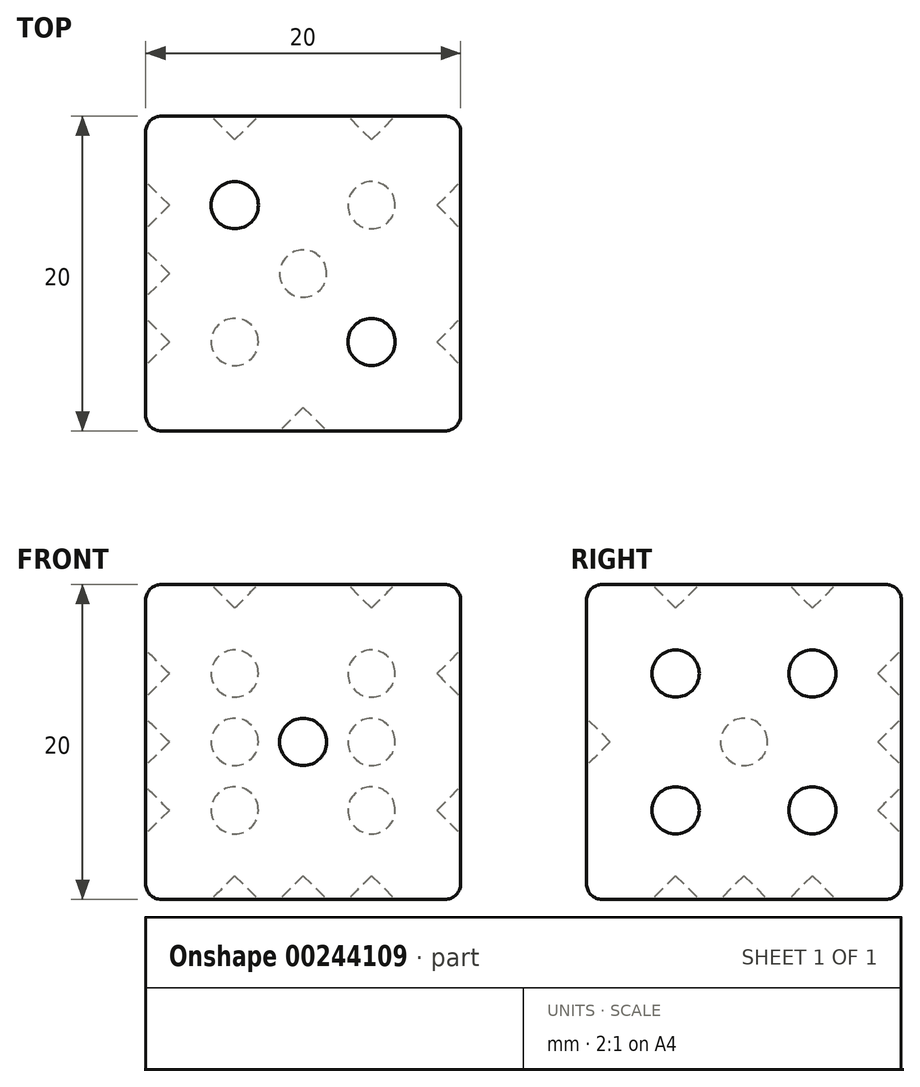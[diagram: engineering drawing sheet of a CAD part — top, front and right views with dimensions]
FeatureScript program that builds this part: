
annotation { "Feature Type Name" : "Feature", "Feature Type Description" : "" }
export const myFeature = defineFeature(function(context is Context, id is Id, definition is map)
    precondition{}
    {
        {
            var Q0;
            Q0=qCreatedBy(makeId("Top.planeOp"),FACE);
            var sketch = newSketch(context, id + "F0", { "sketchPlane" : qUnion([Q0])});
            skLineSegment(sketch, "E0.bottom", {"start": v(0, 0) * mm, "end": v(20, 0) * mm});
            skLineSegment(sketch, "E0.top", {"start": v(0, 20) * mm, "end": v(20, 20) * mm});
            skLineSegment(sketch, "E0.left", {"start": v(0, 0) * mm, "end": v(0, 20) * mm});
            skLineSegment(sketch, "E0.right", {"start": v(20, 0) * mm, "end": v(20, 20) * mm});
            skSolve(sketch);
        }
        {
            var Q0;
            Q0 = qSketchRegion(id + "F0", true);
            extrude(context, id + "F1", {"entities" : qUnion([Q0]), "depth" : 20 * mm});
        }
        {
            var Q0;
            Q0=makeQuery(id+"F1.opExtrude","SWEPT_FACE",FACE,{"disambiguationData":[OSD([sQuery(id+"F0.wireOp",EDGE,"E0.bottom")])]});
            var sketch = newSketch(context, id + "F2", { "sketchPlane" : qUnion([Q0])});
            skLineSegment(sketch, "E1", {"start": v(10, 20) * mm, "end": v(10, 0) * mm, "construction": true});
            skCircle(sketch, "E2", {"center": v(10, 10) * mm, "radius": 1.5 * mm});
            skSolve(sketch);
        }
        {
            var Q0;
            Q0 = qSketchRegion(id + "F2", true);
            extrude(context, id + "F3", {"entities" : qUnion([Q0]), "operationType" : NewBodyOperationType.REMOVE, "oppositeDirection" : true, "depth" : 1.5 * mm});
        }
        {
            var Q0;
            Q0=makeQuery(id+"F3.boolean.opBoolean","COPY",EDGE,{"derivedFrom":makeQuery(id+"F3.opExtrude","CAP_EDGE",EDGE,{"disambiguationData":[OSD([sQuery(id+"F2.wireOp",EDGE,"E2")])],"isStart":false})});
            chamfer(context, id + "F4", {"entities" : qUnion([Q0]), "width" : 1.5 * mm, "tangentPropagation" : true});
        }
        {
            var Q0;
            Q0=makeQuery(id+"F1.opExtrude","CAP_FACE",FACE,{"disambiguationData":[OSD([sQuery(id+"F0.wireOp",EDGE,"E0.bottom"),sQuery(id+"F0.wireOp",EDGE,"E0.top"),sQuery(id+"F0.wireOp",EDGE,"E0.left"),sQuery(id+"F0.wireOp",EDGE,"E0.right")])],"isStart":false});
            var sketch = newSketch(context, id + "F5", { "sketchPlane" : qUnion([Q0])});
            skLineSegment(sketch, "E3", {"start": v(20, 0) * mm, "end": v(14.34, 5.66) * mm, "construction": true});
            skLineSegment(sketch, "E4", {"start": v(0, 20) * mm, "end": v(5.66, 14.34) * mm, "construction": true});
            skCircle(sketch, "E5", {"center": v(5.66, 14.34) * mm, "radius": 1.5 * mm});
            skCircle(sketch, "E6", {"center": v(14.34, 5.66) * mm, "radius": 1.5 * mm});
            skSolve(sketch);
        }
        {
            var Q0;
            Q0=makeQuery(id+"F5.imprint","IMPRINT",FACE,{"disambiguationData":[TD([[makeQuery(id+"F5.imprint","IMPRINT",EDGE,{"derivedFrom":sQuery(id+"F5.wireOp",EDGE,"E5")}),1.0]])]});
            var Q1;
            Q1=makeQuery(id+"F5.imprint","IMPRINT",FACE,{"disambiguationData":[TD([[makeQuery(id+"F5.imprint","IMPRINT",EDGE,{"derivedFrom":sQuery(id+"F5.wireOp",EDGE,"E6")}),1.0]])]});
            extrude(context, id + "F6", {"entities" : qUnion([Q0, Q1]), "operationType" : NewBodyOperationType.REMOVE, "oppositeDirection" : true, "depth" : 1.5 * mm});
        }
        {
            var Q0;
            Q0=makeQuery(id+"F6.boolean.opBoolean","COPY",FACE,{"derivedFrom":makeQuery(id+"F6.opExtrude","CAP_FACE",FACE,{"disambiguationData":[OSD([sQuery(id+"F5.wireOp",EDGE,"E5")])],"isStart":false})});
            chamfer(context, id + "F7", {"entities" : qUnion([Q0]), "width" : 1.5 * mm, "tangentPropagation" : true});
        }
        {
            var Q0;
            Q0=makeQuery(id+"F6.boolean.opBoolean","COPY",FACE,{"derivedFrom":makeQuery(id+"F6.opExtrude","CAP_FACE",FACE,{"disambiguationData":[OSD([sQuery(id+"F5.wireOp",EDGE,"E6")])],"isStart":false})});
            chamfer(context, id + "F8", {"entities" : qUnion([Q0]), "width" : 1.5 * mm, "tangentPropagation" : true});
        }
        {
            var Q0;
            Q0=makeQuery(id+"F1.opExtrude","SWEPT_FACE",FACE,{"disambiguationData":[OSD([sQuery(id+"F0.wireOp",EDGE,"E0.left")])]});
            var sketch = newSketch(context, id + "F9", { "sketchPlane" : qUnion([Q0])});
            skCircle(sketch, "E7", {"center": v(-14.34, 14.34) * mm, "radius": 1.5 * mm});
            skCircle(sketch, "E8", {"center": v(-5.66, 5.66) * mm, "radius": 1.5 * mm});
            skCircle(sketch, "E9", {"center": v(-10, 10) * mm, "radius": 1.5 * mm});
            skSolve(sketch);
        }
        {
            var Q0;
            Q0=makeQuery(id+"F9.imprint","IMPRINT",FACE,{"disambiguationData":[TD([[makeQuery(id+"F9.imprint","IMPRINT",EDGE,{"derivedFrom":sQuery(id+"F9.wireOp",EDGE,"E7")}),1.0]])]});
            var Q1;
            Q1=makeQuery(id+"F9.imprint","IMPRINT",FACE,{"disambiguationData":[TD([[makeQuery(id+"F9.imprint","IMPRINT",EDGE,{"derivedFrom":sQuery(id+"F9.wireOp",EDGE,"E9")}),1.0]])]});
            var Q2;
            Q2=makeQuery(id+"F9.imprint","IMPRINT",FACE,{"disambiguationData":[TD([[makeQuery(id+"F9.imprint","IMPRINT",EDGE,{"derivedFrom":sQuery(id+"F9.wireOp",EDGE,"E8")}),1.0]])]});
            extrude(context, id + "F10", {"entities" : qUnion([Q0, Q1, Q2]), "operationType" : NewBodyOperationType.REMOVE, "oppositeDirection" : true, "depth" : 1.5 * mm});
        }
        {
            var Q0;
            Q0=makeQuery(id+"F10.boolean.opBoolean","COPY",FACE,{"derivedFrom":makeQuery(id+"F10.opExtrude","CAP_FACE",FACE,{"disambiguationData":[OSD([sQuery(id+"F9.wireOp",EDGE,"E7")])],"isStart":false})});
            var Q1;
            Q1=makeQuery(id+"F10.boolean.opBoolean","COPY",FACE,{"derivedFrom":makeQuery(id+"F10.opExtrude","CAP_FACE",FACE,{"disambiguationData":[OSD([sQuery(id+"F9.wireOp",EDGE,"E9")])],"isStart":false})});
            var Q2;
            Q2=makeQuery(id+"F10.boolean.opBoolean","COPY",FACE,{"derivedFrom":makeQuery(id+"F10.opExtrude","CAP_FACE",FACE,{"disambiguationData":[OSD([sQuery(id+"F9.wireOp",EDGE,"E8")])],"isStart":false})});
            chamfer(context, id + "F11", {"entities" : qUnion([Q0, Q1, Q2]), "width" : 1.5 * mm, "tangentPropagation" : true});
        }
        {
            var Q0;
            Q0=makeQuery(id+"F1.opExtrude","SWEPT_FACE",FACE,{"disambiguationData":[OSD([sQuery(id+"F0.wireOp",EDGE,"E0.right")])]});
            var sketch = newSketch(context, id + "F12", { "sketchPlane" : qUnion([Q0])});
            skCircle(sketch, "E10", {"center": v(5.66, 14.34) * mm, "radius": 1.5 * mm});
            skCircle(sketch, "E11", {"center": v(14.34, 14.34) * mm, "radius": 1.5 * mm});
            skCircle(sketch, "E12", {"center": v(14.34, 5.66) * mm, "radius": 1.5 * mm});
            skCircle(sketch, "E13", {"center": v(5.66, 5.66) * mm, "radius": 1.5 * mm});
            skSolve(sketch);
        }
        {
            var Q0;
            Q0=makeQuery(id+"F12.imprint","IMPRINT",FACE,{"disambiguationData":[TD([[makeQuery(id+"F12.imprint","IMPRINT",EDGE,{"derivedFrom":sQuery(id+"F12.wireOp",EDGE,"E10")}),1.0]])]});
            var Q1;
            Q1=makeQuery(id+"F12.imprint","IMPRINT",FACE,{"disambiguationData":[TD([[makeQuery(id+"F12.imprint","IMPRINT",EDGE,{"derivedFrom":sQuery(id+"F12.wireOp",EDGE,"E11")}),1.0]])]});
            var Q2;
            Q2=makeQuery(id+"F12.imprint","IMPRINT",FACE,{"disambiguationData":[TD([[makeQuery(id+"F12.imprint","IMPRINT",EDGE,{"derivedFrom":sQuery(id+"F12.wireOp",EDGE,"E12")}),1.0]])]});
            var Q3;
            Q3=makeQuery(id+"F12.imprint","IMPRINT",FACE,{"disambiguationData":[TD([[makeQuery(id+"F12.imprint","IMPRINT",EDGE,{"derivedFrom":sQuery(id+"F12.wireOp",EDGE,"E13")}),1.0]])]});
            extrude(context, id + "F13", {"entities" : qUnion([Q0, Q1, Q2, Q3]), "operationType" : NewBodyOperationType.REMOVE, "oppositeDirection" : true, "depth" : 1.5 * mm});
        }
        {
            var Q0;
            Q0=makeQuery(id+"F13.boolean.opBoolean","COPY",FACE,{"derivedFrom":makeQuery(id+"F13.opExtrude","CAP_FACE",FACE,{"disambiguationData":[OSD([sQuery(id+"F12.wireOp",EDGE,"E10")])],"isStart":false})});
            var Q1;
            Q1=makeQuery(id+"F13.boolean.opBoolean","COPY",FACE,{"derivedFrom":makeQuery(id+"F13.opExtrude","CAP_FACE",FACE,{"disambiguationData":[OSD([sQuery(id+"F12.wireOp",EDGE,"E11")])],"isStart":false})});
            var Q2;
            Q2=makeQuery(id+"F13.boolean.opBoolean","COPY",FACE,{"derivedFrom":makeQuery(id+"F13.opExtrude","CAP_FACE",FACE,{"disambiguationData":[OSD([sQuery(id+"F12.wireOp",EDGE,"E12")])],"isStart":false})});
            var Q3;
            Q3=makeQuery(id+"F13.boolean.opBoolean","COPY",FACE,{"derivedFrom":makeQuery(id+"F13.opExtrude","CAP_FACE",FACE,{"disambiguationData":[OSD([sQuery(id+"F12.wireOp",EDGE,"E13")])],"isStart":false})});
            chamfer(context, id + "F14", {"entities" : qUnion([Q0, Q1, Q2, Q3]), "width" : 1.5 * mm, "tangentPropagation" : true});
        }
        {
            var Q0;
            Q0=makeQuery(id+"F1.opExtrude","CAP_FACE",FACE,{"disambiguationData":[OSD([sQuery(id+"F0.wireOp",EDGE,"E0.bottom"),sQuery(id+"F0.wireOp",EDGE,"E0.top"),sQuery(id+"F0.wireOp",EDGE,"E0.left"),sQuery(id+"F0.wireOp",EDGE,"E0.right")])],"isStart":true});
            var sketch = newSketch(context, id + "F15", { "sketchPlane" : qUnion([Q0])});
            skCircle(sketch, "E14", {"center": v(5.66, -5.66) * mm, "radius": 1.5 * mm});
            skCircle(sketch, "E15", {"center": v(14.34, -5.66) * mm, "radius": 1.5 * mm});
            skCircle(sketch, "E16", {"center": v(14.34, -14.34) * mm, "radius": 1.5 * mm});
            skCircle(sketch, "E17", {"center": v(5.66, -14.34) * mm, "radius": 1.5 * mm});
            skCircle(sketch, "E18", {"center": v(10, -10) * mm, "radius": 1.5 * mm});
            skSolve(sketch);
        }
        {
            var Q0;
            Q0=makeQuery(id+"F15.imprint","IMPRINT",FACE,{"disambiguationData":[TD([[makeQuery(id+"F15.imprint","IMPRINT",EDGE,{"derivedFrom":sQuery(id+"F15.wireOp",EDGE,"E14")}),1.0]])]});
            var Q1;
            Q1=makeQuery(id+"F15.imprint","IMPRINT",FACE,{"disambiguationData":[TD([[makeQuery(id+"F15.imprint","IMPRINT",EDGE,{"derivedFrom":sQuery(id+"F15.wireOp",EDGE,"E18")}),1.0]])]});
            var Q2;
            Q2=makeQuery(id+"F15.imprint","IMPRINT",FACE,{"disambiguationData":[TD([[makeQuery(id+"F15.imprint","IMPRINT",EDGE,{"derivedFrom":sQuery(id+"F15.wireOp",EDGE,"E15")}),1.0]])]});
            var Q3;
            Q3=makeQuery(id+"F15.imprint","IMPRINT",FACE,{"disambiguationData":[TD([[makeQuery(id+"F15.imprint","IMPRINT",EDGE,{"derivedFrom":sQuery(id+"F15.wireOp",EDGE,"E16")}),1.0]])]});
            var Q4;
            Q4=makeQuery(id+"F15.imprint","IMPRINT",FACE,{"disambiguationData":[TD([[makeQuery(id+"F15.imprint","IMPRINT",EDGE,{"derivedFrom":sQuery(id+"F15.wireOp",EDGE,"E17")}),1.0]])]});
            extrude(context, id + "F16", {"entities" : qUnion([Q0, Q1, Q2, Q3, Q4]), "operationType" : NewBodyOperationType.REMOVE, "oppositeDirection" : true, "depth" : 1.5 * mm});
        }
        {
            var Q0;
            Q0=makeQuery(id+"F16.boolean.opBoolean","COPY",FACE,{"derivedFrom":makeQuery(id+"F16.opExtrude","CAP_FACE",FACE,{"disambiguationData":[OSD([sQuery(id+"F15.wireOp",EDGE,"E14")])],"isStart":false})});
            var Q1;
            Q1=makeQuery(id+"F16.boolean.opBoolean","COPY",FACE,{"derivedFrom":makeQuery(id+"F16.opExtrude","CAP_FACE",FACE,{"disambiguationData":[OSD([sQuery(id+"F15.wireOp",EDGE,"E15")])],"isStart":false})});
            var Q2;
            Q2=makeQuery(id+"F16.boolean.opBoolean","COPY",FACE,{"derivedFrom":makeQuery(id+"F16.opExtrude","CAP_FACE",FACE,{"disambiguationData":[OSD([sQuery(id+"F15.wireOp",EDGE,"E18")])],"isStart":false})});
            var Q3;
            Q3=makeQuery(id+"F16.boolean.opBoolean","COPY",FACE,{"derivedFrom":makeQuery(id+"F16.opExtrude","CAP_FACE",FACE,{"disambiguationData":[OSD([sQuery(id+"F15.wireOp",EDGE,"E17")])],"isStart":false})});
            var Q4;
            Q4=makeQuery(id+"F16.boolean.opBoolean","COPY",FACE,{"derivedFrom":makeQuery(id+"F16.opExtrude","CAP_FACE",FACE,{"disambiguationData":[OSD([sQuery(id+"F15.wireOp",EDGE,"E16")])],"isStart":false})});
            chamfer(context, id + "F17", {"entities" : qUnion([Q0, Q1, Q2, Q3, Q4]), "width" : 1.5 * mm, "tangentPropagation" : true});
        }
        {
            var Q0;
            Q0=makeQuery(id+"F1.opExtrude","SWEPT_FACE",FACE,{"disambiguationData":[OSD([sQuery(id+"F0.wireOp",EDGE,"E0.top")])]});
            var sketch = newSketch(context, id + "F18", { "sketchPlane" : qUnion([Q0])});
            skCircle(sketch, "E19", {"center": v(-14.34, 14.34) * mm, "radius": 1.5 * mm});
            skCircle(sketch, "E20", {"center": v(-5.66, 14.34) * mm, "radius": 1.5 * mm});
            skCircle(sketch, "E21", {"center": v(-5.66, 5.66) * mm, "radius": 1.5 * mm});
            skCircle(sketch, "E22", {"center": v(-14.34, 5.66) * mm, "radius": 1.5 * mm});
            skCircle(sketch, "E23", {"center": v(-14.34, 10) * mm, "radius": 1.5 * mm});
            skCircle(sketch, "E24", {"center": v(-5.66, 10) * mm, "radius": 1.5 * mm});
            skSolve(sketch);
        }
        {
            var Q0;
            Q0=makeQuery(id+"F18.imprint","IMPRINT",FACE,{"disambiguationData":[TD([[makeQuery(id+"F18.imprint","IMPRINT",EDGE,{"derivedFrom":sQuery(id+"F18.wireOp",EDGE,"E19")}),1.0]])]});
            var Q1;
            Q1=makeQuery(id+"F18.imprint","IMPRINT",FACE,{"disambiguationData":[TD([[makeQuery(id+"F18.imprint","IMPRINT",EDGE,{"derivedFrom":sQuery(id+"F18.wireOp",EDGE,"E20")}),1.0]])]});
            var Q2;
            Q2=makeQuery(id+"F18.imprint","IMPRINT",FACE,{"disambiguationData":[TD([[makeQuery(id+"F18.imprint","IMPRINT",EDGE,{"derivedFrom":sQuery(id+"F18.wireOp",EDGE,"E24")}),1.0]])]});
            var Q3;
            Q3=makeQuery(id+"F18.imprint","IMPRINT",FACE,{"disambiguationData":[TD([[makeQuery(id+"F18.imprint","IMPRINT",EDGE,{"derivedFrom":sQuery(id+"F18.wireOp",EDGE,"E23")}),1.0]])]});
            var Q4;
            Q4=makeQuery(id+"F18.imprint","IMPRINT",FACE,{"disambiguationData":[TD([[makeQuery(id+"F18.imprint","IMPRINT",EDGE,{"derivedFrom":sQuery(id+"F18.wireOp",EDGE,"E22")}),1.0]])]});
            var Q5;
            Q5=makeQuery(id+"F18.imprint","IMPRINT",FACE,{"disambiguationData":[TD([[makeQuery(id+"F18.imprint","IMPRINT",EDGE,{"derivedFrom":sQuery(id+"F18.wireOp",EDGE,"E21")}),1.0]])]});
            extrude(context, id + "F19", {"entities" : qUnion([Q0, Q1, Q2, Q3, Q4, Q5]), "operationType" : NewBodyOperationType.REMOVE, "oppositeDirection" : true, "depth" : 1.5 * mm});
        }
        {
            var Q0;
            Q0=makeQuery(id+"F19.boolean.opBoolean","COPY",FACE,{"derivedFrom":makeQuery(id+"F19.opExtrude","CAP_FACE",FACE,{"disambiguationData":[OSD([sQuery(id+"F18.wireOp",EDGE,"E19")])],"isStart":false})});
            var Q1;
            Q1=makeQuery(id+"F19.boolean.opBoolean","COPY",FACE,{"derivedFrom":makeQuery(id+"F19.opExtrude","CAP_FACE",FACE,{"disambiguationData":[OSD([sQuery(id+"F18.wireOp",EDGE,"E20")])],"isStart":false})});
            var Q2;
            Q2=makeQuery(id+"F19.boolean.opBoolean","COPY",FACE,{"derivedFrom":makeQuery(id+"F19.opExtrude","CAP_FACE",FACE,{"disambiguationData":[OSD([sQuery(id+"F18.wireOp",EDGE,"E24")])],"isStart":false})});
            var Q3;
            Q3=makeQuery(id+"F19.boolean.opBoolean","COPY",FACE,{"derivedFrom":makeQuery(id+"F19.opExtrude","CAP_FACE",FACE,{"disambiguationData":[OSD([sQuery(id+"F18.wireOp",EDGE,"E23")])],"isStart":false})});
            var Q4;
            Q4=makeQuery(id+"F19.boolean.opBoolean","COPY",FACE,{"derivedFrom":makeQuery(id+"F19.opExtrude","CAP_FACE",FACE,{"disambiguationData":[OSD([sQuery(id+"F18.wireOp",EDGE,"E22")])],"isStart":false})});
            var Q5;
            Q5=makeQuery(id+"F19.boolean.opBoolean","COPY",FACE,{"derivedFrom":makeQuery(id+"F19.opExtrude","CAP_FACE",FACE,{"disambiguationData":[OSD([sQuery(id+"F18.wireOp",EDGE,"E21")])],"isStart":false})});
            chamfer(context, id + "F20", {"entities" : qUnion([Q0, Q1, Q2, Q3, Q4, Q5]), "width" : 1.5 * mm, "tangentPropagation" : true});
        }
        {
            var Q0;
            Q0=makeQuery(id+"F1.opExtrude","CAP_EDGE",EDGE,{"disambiguationData":[OSD([sQuery(id+"F0.wireOp",EDGE,"E0.left")])],"isStart":false});
            var Q1;
            Q1=makeQuery(id+"F1.opExtrude","CAP_EDGE",EDGE,{"disambiguationData":[OSD([sQuery(id+"F0.wireOp",EDGE,"E0.bottom")])],"isStart":false});
            var Q2;
            Q2=makeQuery(id+"F1.opExtrude","CAP_EDGE",EDGE,{"disambiguationData":[OSD([sQuery(id+"F0.wireOp",EDGE,"E0.right")])],"isStart":false});
            var Q3;
            Q3=makeQuery(id+"F1.opExtrude","CAP_EDGE",EDGE,{"disambiguationData":[OSD([sQuery(id+"F0.wireOp",EDGE,"E0.top")])],"isStart":false});
            var Q4;
            Q4=makeQuery(id+"F1.opExtrude","SWEPT_EDGE",EDGE,{"disambiguationData":[OSD([sQuery(id+"F0.wireOp",EDGE,"E0.top"),sQuery(id+"F0.wireOp",EDGE,"E0.right")])]});
            var Q5;
            Q5=makeQuery(id+"F1.opExtrude","SWEPT_EDGE",EDGE,{"disambiguationData":[OSD([sQuery(id+"F0.wireOp",EDGE,"E0.bottom"),sQuery(id+"F0.wireOp",EDGE,"E0.right")])]});
            var Q6;
            Q6=makeQuery(id+"F1.opExtrude","SWEPT_EDGE",EDGE,{"disambiguationData":[OSD([sQuery(id+"F0.wireOp",EDGE,"E0.bottom"),sQuery(id+"F0.wireOp",EDGE,"E0.left")])]});
            var Q7;
            Q7=makeQuery(id+"F1.opExtrude","CAP_EDGE",EDGE,{"disambiguationData":[OSD([sQuery(id+"F0.wireOp",EDGE,"E0.right")])],"isStart":true});
            var Q8;
            Q8=makeQuery(id+"F1.opExtrude","CAP_EDGE",EDGE,{"disambiguationData":[OSD([sQuery(id+"F0.wireOp",EDGE,"E0.bottom")])],"isStart":true});
            var Q9;
            Q9=makeQuery(id+"F1.opExtrude","SWEPT_EDGE",EDGE,{"disambiguationData":[OSD([sQuery(id+"F0.wireOp",EDGE,"E0.top"),sQuery(id+"F0.wireOp",EDGE,"E0.left")])]});
            var Q10;
            Q10=makeQuery(id+"F1.opExtrude","CAP_EDGE",EDGE,{"disambiguationData":[OSD([sQuery(id+"F0.wireOp",EDGE,"E0.left")])],"isStart":true});
            var Q11;
            Q11=makeQuery(id+"F1.opExtrude","CAP_EDGE",EDGE,{"disambiguationData":[OSD([sQuery(id+"F0.wireOp",EDGE,"E0.top")])],"isStart":true});
            fillet(context, id + "F21", {"entities" : qUnion([Q0, Q1, Q2, Q3, Q4, Q5, Q6, Q7, Q8, Q9, Q10, Q11]), "radius" : 1 * mm, "tangentPropagation" : true, "allowEdgeOverflow" : false});
        }
    });
